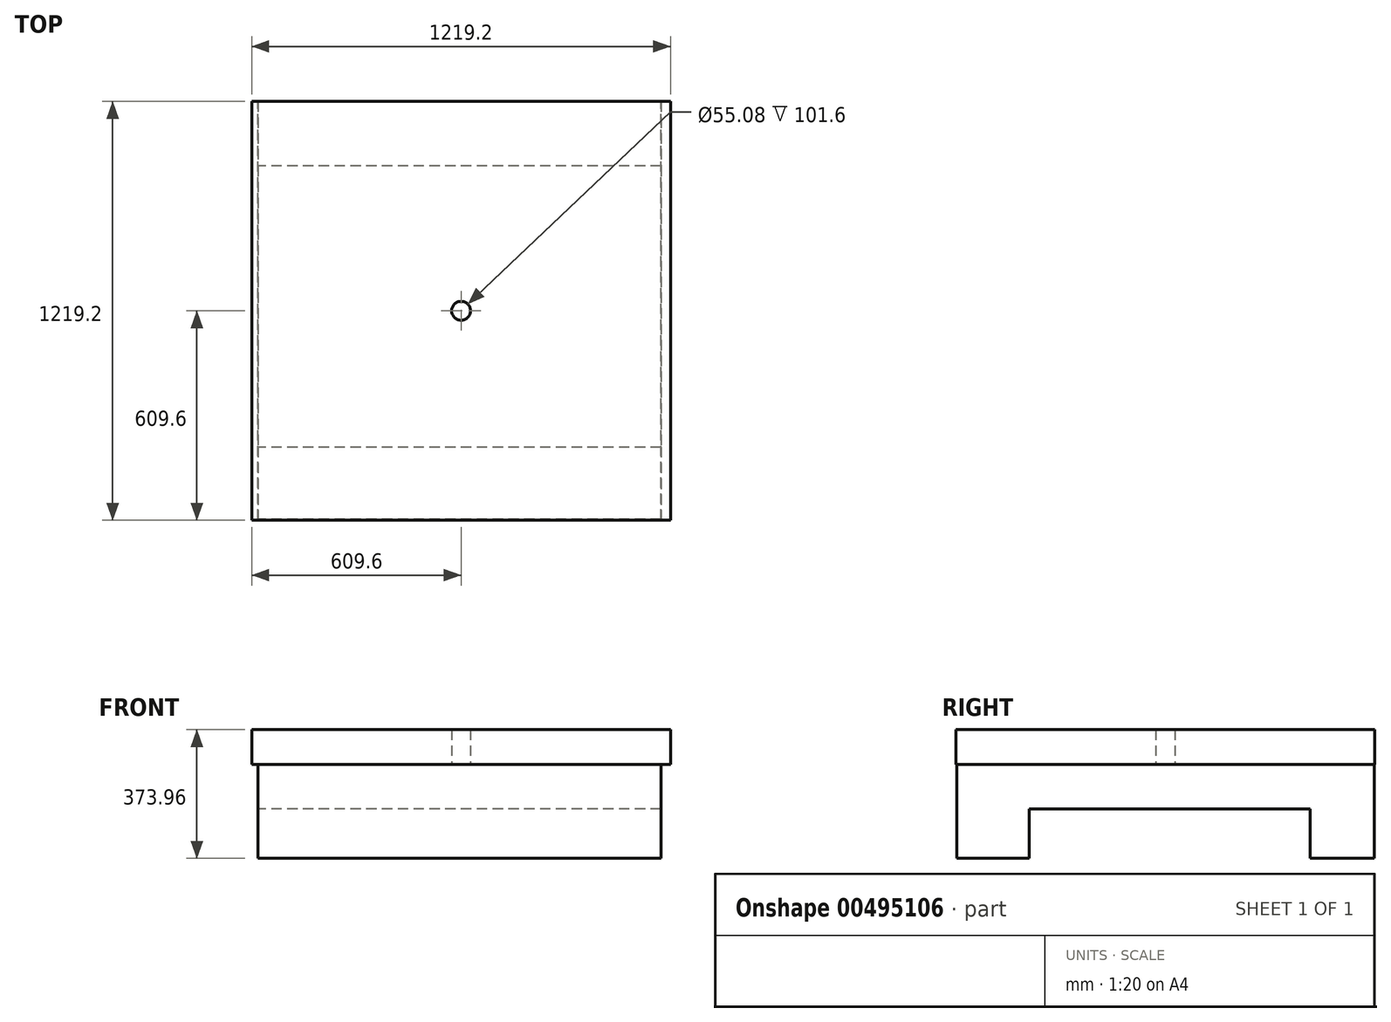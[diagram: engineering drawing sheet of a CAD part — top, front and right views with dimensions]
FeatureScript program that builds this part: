
annotation { "Feature Type Name" : "Feature", "Feature Type Description" : "" }
export const myFeature = defineFeature(function(context is Context, id is Id, definition is map)
    precondition{}
    {
        {
            var Q0;
            Q0=qCreatedBy(makeId("Top.planeOp"),FACE);
            var sketch = newSketch(context, id + "F0", { "sketchPlane" : qUnion([Q0])});
            skLineSegment(sketch, "E0", {"start": v(609.6, 609.6) * mm, "end": v(-609.6, 609.6) * mm});
            skLineSegment(sketch, "E1", {"start": v(-609.6, 609.6) * mm, "end": v(-609.6, -609.6) * mm});
            skLineSegment(sketch, "E2", {"start": v(-609.6, -609.6) * mm, "end": v(609.6, -609.6) * mm});
            skLineSegment(sketch, "E3", {"start": v(609.6, -609.6) * mm, "end": v(609.6, 609.6) * mm});
            skPoint(sketch, "E4.centerSnap0", {"position": v(-609.6, 0) * mm});
            skPoint(sketch, "E4.centerSnap1", {"position": v(0, 609.6) * mm});
            skCircle(sketch, "E5", {"center": v(0, 0) * mm, "radius": 27.49 * mm});
            skCircle(sketch, "E6", {"center": v(0, 0) * mm, "radius": 27.54 * mm});
            skSolve(sketch);
        }
        {
            var Q0;
            Q0=makeQuery(id+"F0.imprint","IMPRINT",FACE,{"disambiguationData":[TD([[makeQuery(id+"F0.imprint","IMPRINT",EDGE,{"derivedFrom":sQuery(id+"F0.wireOp",EDGE,"E0")}),1.0]])]});
            extrude(context, id + "F1", {"entities" : qUnion([Q0]), "depth" : 101.6 * mm});
        }
        {
            var Q0;
            Q0=qCreatedBy(makeId("Right.planeOp"),FACE);
            var sketch = newSketch(context, id + "F2", { "sketchPlane" : qUnion([Q0])});
            skLineSegment(sketch, "E7", {"start": v(608.82, 0) * mm, "end": v(608.82, -272.36) * mm});
            skLineSegment(sketch, "E8", {"start": v(608.82, -272.36) * mm, "end": v(-607.33, -272.36) * mm});
            skLineSegment(sketch, "E9", {"start": v(-607.33, -272.36) * mm, "end": v(-607.33, 0) * mm});
            skLineSegment(sketch, "E10", {"start": v(-607.33, 0) * mm, "end": v(608.82, 0) * mm});
            skLineSegment(sketch, "E11.bottom", {"start": v(421.26, -272.36) * mm, "end": v(-396.7, -272.36) * mm});
            skLineSegment(sketch, "E11.top", {"start": v(421.26, -129.46) * mm, "end": v(-396.7, -129.46) * mm});
            skLineSegment(sketch, "E11.left", {"start": v(421.26, -272.36) * mm, "end": v(421.26, -129.46) * mm});
            skLineSegment(sketch, "E11.right", {"start": v(-396.7, -272.36) * mm, "end": v(-396.7, -129.46) * mm});
            skSolve(sketch);
        }
        {
            var Q0;
            {var subQ4=sQuery(id+"F2.wireOp",EDGE,"E7");Q0=makeQuery(id+"F2.imprint","IMPRINT",FACE,{"disambiguationData":[TD([[makeQuery(id+"F2.imprint","IMPRINT",EDGE,{"derivedFrom":subQ4}),-1.0]])]});}
            extrude(context, id + "F3", {"entities" : qUnion([Q0]), "operationType" : NewBodyOperationType.ADD, "depth" : 581.66 * mm, "hasSecondDirection" : true, "secondDirectionOppositeDirection" : true, "secondDirectionDepth" : 591.82 * mm});
        }
    });
